# Revit family: EVC Series
name_source: partatom
category: Lighting Fixtures
revit_build: Autodesk Revit Architecture 2012 (Build: 20110309_2315(x64)
units: mm (PartAtom-declared; Revit-internal decimal feet)

## types (2) — shared parameters
Apparent Load = 0 VA
Color Filter = 16777215
Default Elevation = 48.000"
Description = The EVC Series is a compact architectural LED combination exit and emergency lighting unit designed for fast installation and reliable service
Dimming Lamp Color Temperature Shift = <None>
Glass = light Glass
Manufacturer = Dual Lighting
Manufacturer Fax = (866)-898-0131
Model = EVC Series
Photometric Web File = generic
Product Documentation Link = http://www.dual-lite.com
Product Page URL = http://www.dual-lite.com
Tilt Angle = 0.00°
Total Input Wattage = 1-3 W
URL = http://www.dual-lite.com
Voltage = 120 V

## per-type parameters (varying)
| type | Emit from Line Length | Finish | Lens |
| EVC-W | 2.000" | White | Red Glass |
| EVC-B | 24.000" | Black | Green Glass |

## geometry (parser evidence)
native form markers: Blend x2, Sweep x6
no freeform markers — native parametric forms only
